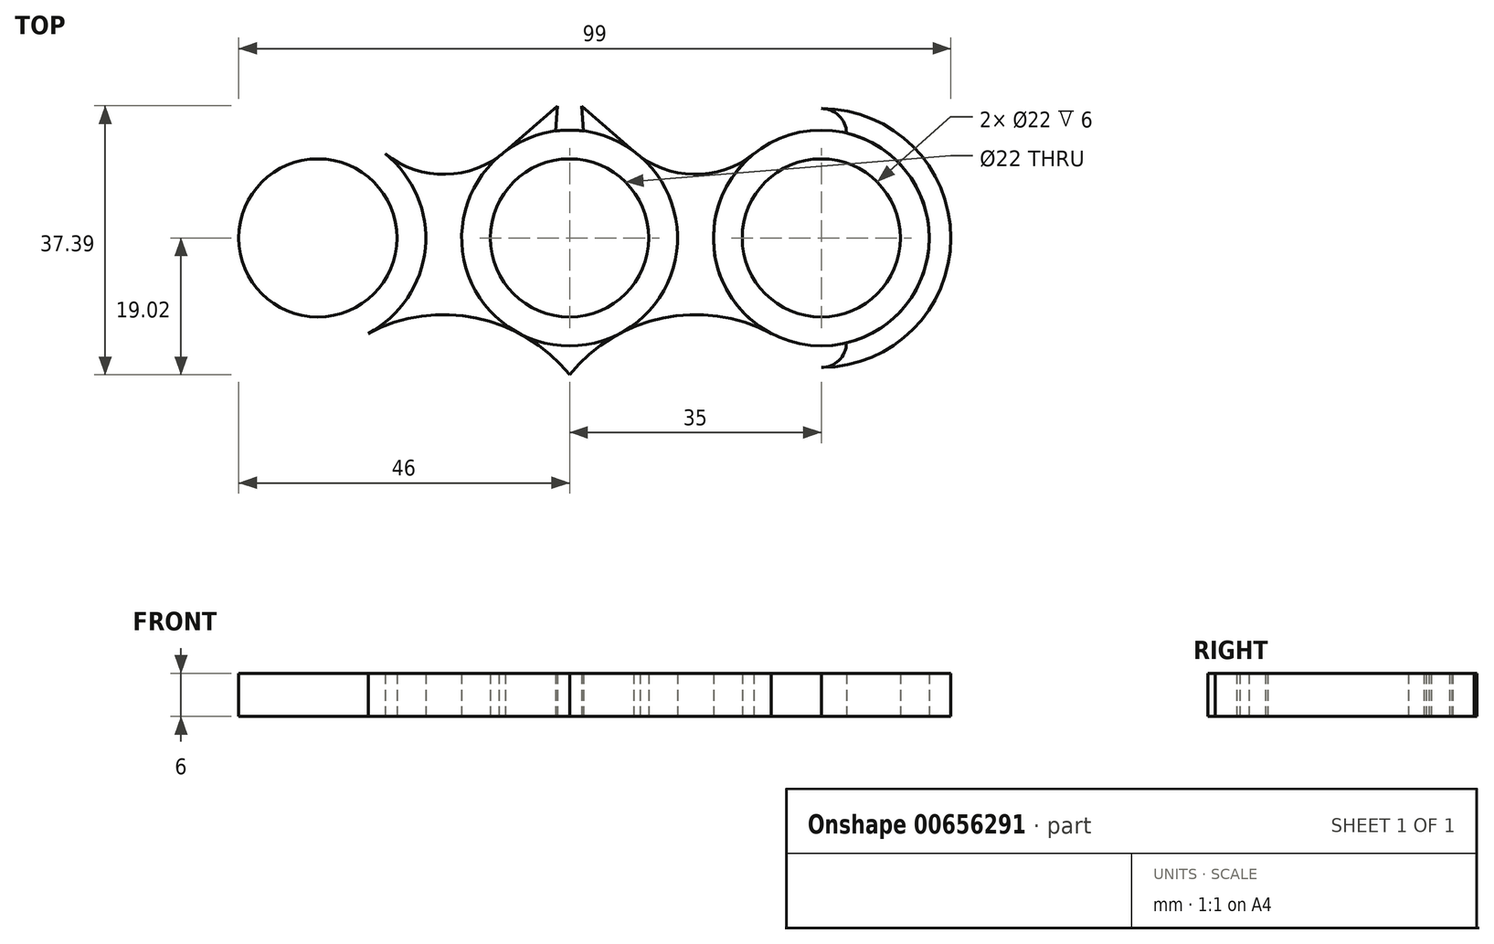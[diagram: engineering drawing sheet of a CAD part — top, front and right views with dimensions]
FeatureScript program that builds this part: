
annotation { "Feature Type Name" : "Feature", "Feature Type Description" : "" }
export const myFeature = defineFeature(function(context is Context, id is Id, definition is map)
    precondition{}
    {
        {
            var Q0;
            Q0=qCreatedBy(makeId("Top.planeOp"),FACE);
            var sketch = newSketch(context, id + "F0", { "sketchPlane" : qUnion([Q0])});
            skCircle(sketch, "E0", {"center": v(0, 0) * mm, "radius": 11 * mm});
            skArc(sketch, "E1", {"start": v(9.79, 11.37) * mm, "mid": v(9.37, 11.71) * mm, "end": v(8.95, 12.04) * mm});
            skLineSegment(sketch, "E2", {"start": v(0, 37.98) * mm, "end": v(0, -39.63) * mm, "construction": true});
            skLineSegment(sketch, "E3", {"start": v(1.92, 14.88) * mm, "end": v(1.68, 18.37) * mm});
            skLineSegment(sketch, "E4", {"start": v(1.68, 18.37) * mm, "end": v(8.95, 12.04) * mm});
            skLineSegment(sketch, "E5.MirrorCS", {"start": v(-1.92, 14.88) * mm, "end": v(-1.68, 18.37) * mm});
            skLineSegment(sketch, "E6.MirrorCS", {"start": v(-1.68, 18.37) * mm, "end": v(-8.95, 12.04) * mm});
            skLineSegment(sketch, "E7", {"start": v(-52.8, 0) * mm, "end": v(68.66, 0) * mm, "construction": true});
            skCircle(sketch, "E8", {"center": v(35, 0) * mm, "radius": 11 * mm});
            skCircle(sketch, "E9.MirrorC", {"center": v(-35, 0) * mm, "radius": 11 * mm});
            skArc(sketch, "E10", {"start": v(28, -13.27) * mm, "mid": v(33.13, -14.88) * mm, "end": v(38.5, -14.59) * mm});
            skArc(sketch, "E11.MirrorC", {"start": v(-38.5, 14.59) * mm, "mid": v(-31.72, 14.64) * mm, "end": v(-25.62, 11.7) * mm});
            skArc(sketch, "E12", {"start": v(8.95, 12.04) * mm, "mid": v(17.22, 8.85) * mm, "end": v(25.62, 11.7) * mm});
            skArc(sketch, "E13.MirrorCS", {"start": v(-8.95, 12.04) * mm, "mid": v(-17.22, 8.85) * mm, "end": v(-25.62, 11.7) * mm});
            skArc(sketch, "E14", {"start": v(0, -19.02) * mm, "mid": v(-12.97, -11.13) * mm, "end": v(-28, -13.27) * mm});
            skArc(sketch, "E15", {"start": v(-20.67, -10.9) * mm, "mid": v(-17.04, -1.14) * mm, "end": v(-19.4, 8.99) * mm});
            skArc(sketch, "E16", {"start": v(-38.5, 14.59) * mm, "mid": v(-37.44, 17) * mm, "end": v(-35, 18) * mm});
            skArc(sketch, "E17.MirrorC", {"start": v(-38.5, -14.59) * mm, "mid": v(-37.44, -17) * mm, "end": v(-35, -18) * mm});
            skArc(sketch, "E18.MirrorC", {"start": v(38.5, 14.59) * mm, "mid": v(37.44, 17) * mm, "end": v(35, 18) * mm});
            skArc(sketch, "E19.MirrorC", {"start": v(38.5, -14.59) * mm, "mid": v(37.44, -17) * mm, "end": v(35, -18) * mm});
            skArc(sketch, "E20.MirrorC", {"start": v(20.67, -10.9) * mm, "mid": v(17.04, -1.14) * mm, "end": v(19.4, 8.99) * mm});
            skArc(sketch, "E21.MirrorCS", {"start": v(0, -19.02) * mm, "mid": v(12.97, -11.13) * mm, "end": v(28, -13.27) * mm});
            skArc(sketch, "E22.trimOffspring", {"start": v(-35, 18) * mm, "mid": v(-53, 0) * mm, "end": v(-35, -18) * mm});
            skArc(sketch, "E23.trimOffspring", {"start": v(-28, -13.27) * mm, "mid": v(-33.13, -14.88) * mm, "end": v(-38.5, -14.59) * mm});
            skArc(sketch, "E24.trimOffspring", {"start": v(35, 18) * mm, "mid": v(53, 0) * mm, "end": v(35, -18) * mm});
            skArc(sketch, "E25.trimOffspring", {"start": v(38.5, 14.59) * mm, "mid": v(31.72, 14.64) * mm, "end": v(25.62, 11.7) * mm});
            skArc(sketch, "E26.trimOffspring", {"start": v(1.92, 14.88) * mm, "mid": v(0, 15) * mm, "end": v(-1.92, 14.88) * mm});
            skCircle(sketch, "E27", {"center": v(0, 0) * mm, "radius": 15 * mm});
            skCircle(sketch, "E28", {"center": v(-35, 0) * mm, "radius": 15 * mm});
            skCircle(sketch, "E29", {"center": v(35, 0) * mm, "radius": 15 * mm});
            skSolve(sketch);
        }
        {
            var Q0;
            Q0=makeQuery(id+"F0.imprint","IMPRINT",FACE,{"disambiguationData":[TD([[makeQuery(id+"F0.imprint","IMPRINT",EDGE,{"derivedFrom":sQuery(id+"F0.wireOp",EDGE,"E0")}),-1.0]])]});
            extrude(context, id + "F1", {"entities" : qUnion([Q0]), "depth" : 6 * mm, "offsetDistance" : 25 * mm});
        }
        {
            var Q0;
            {var subQ0=sQuery(id+"F0.wireOp",EDGE,"E16");Q0=makeQuery(id+"F0.imprint","IMPRINT",FACE,{"disambiguationData":[TD([[makeQuery(id+"F0.imprint","IMPRINT",EDGE,{"derivedFrom":subQ0}),1.0]])]});}
            var Q1;
            {var subQ3=sQuery(id+"F0.wireOp",EDGE,"E15");Q1=makeQuery(id+"F0.imprint","IMPRINT",FACE,{"disambiguationData":[TD([[makeQuery(id+"F0.imprint","IMPRINT",EDGE,{"derivedFrom":subQ3}),1.0]])]});}
            var Q2;
            {var subQ0=sQuery(id+"F0.wireOp",EDGE,"E15");Q2=makeQuery(id+"F0.imprint","IMPRINT",FACE,{"disambiguationData":[TD([[makeQuery(id+"F0.imprint","IMPRINT",EDGE,{"derivedFrom":subQ0}),-1.0]])]});}
            var Q3;
            Q3=makeQuery(id+"F0.imprint","IMPRINT",FACE,{"disambiguationData":[TD([[makeQuery(id+"F0.imprint","IMPRINT",EDGE,{"derivedFrom":sQuery(id+"F0.wireOp",EDGE,"E0")}),-1.0]])]});
            var Q4;
            {var subQ0=sQuery(id+"F0.wireOp",EDGE,"E21.MirrorCS");var subQ1=sQuery(id+"F0.wireOp",EDGE,"E14");var subQ2=makeQuery(id+"F0.imprint","INTERSECT",VERTEX,{"derivedFrom":[subQ1,subQ0]});Q4=makeQuery(id+"F0.imprint","IMPRINT",FACE,{"disambiguationData":[TD([[makeQuery(id+"F0.imprint","IMPRINT",EDGE,{"disambiguationData":[TD([[subQ2,-1.0]])],"derivedFrom":subQ1}),-1.0]])]});}
            var Q5;
            {var subQ0=sQuery(id+"F0.wireOp",EDGE,"E20.MirrorC");Q5=makeQuery(id+"F0.imprint","IMPRINT",FACE,{"disambiguationData":[TD([[makeQuery(id+"F0.imprint","IMPRINT",EDGE,{"derivedFrom":subQ0}),1.0]])]});}
            var Q6;
            {var subQ3=sQuery(id+"F0.wireOp",EDGE,"E20.MirrorC");Q6=makeQuery(id+"F0.imprint","IMPRINT",FACE,{"disambiguationData":[TD([[makeQuery(id+"F0.imprint","IMPRINT",EDGE,{"derivedFrom":subQ3}),-1.0]])]});}
            var Q7;
            {var subQ0=sQuery(id+"F0.wireOp",EDGE,"E18.MirrorC");Q7=makeQuery(id+"F0.imprint","IMPRINT",FACE,{"disambiguationData":[TD([[makeQuery(id+"F0.imprint","IMPRINT",EDGE,{"derivedFrom":subQ0}),-1.0]])]});}
            var Q8;
            {var subQ0=sQuery(id+"F0.wireOp",EDGE,"E5.MirrorCS");Q8=makeQuery(id+"F0.imprint","IMPRINT",FACE,{"disambiguationData":[TD([[makeQuery(id+"F0.imprint","IMPRINT",EDGE,{"derivedFrom":subQ0}),1.0]])]});}
            var Q9;
            {var subQ0=sQuery(id+"F0.wireOp",EDGE,"E3");Q9=makeQuery(id+"F0.imprint","IMPRINT",FACE,{"disambiguationData":[TD([[makeQuery(id+"F0.imprint","IMPRINT",EDGE,{"derivedFrom":subQ0}),-1.0]])]});}
            extrude(context, id + "F2", {"entities" : qUnion([Q0, Q1, Q2, Q3, Q4, Q5, Q6, Q7, Q8, Q9]), "depth" : 6 * mm, "offsetDistance" : 25 * mm});
        }
        {
            var Q0;
            Q0=makeQuery(id+"F0.imprint","IMPRINT",FACE,{"disambiguationData":[TD([[makeQuery(id+"F0.imprint","IMPRINT",EDGE,{"derivedFrom":sQuery(id+"F0.wireOp",EDGE,"E8")}),-1.0]])]});
            var Q1;
            Q1=makeQuery(id+"F0.imprint","IMPRINT",FACE,{"disambiguationData":[TD([[makeQuery(id+"F0.imprint","IMPRINT",EDGE,{"derivedFrom":sQuery(id+"F0.wireOp",EDGE,"E9.MirrorC")}),1.0]])]});
            extrude(context, id + "F3", {"entities" : qUnion([Q0, Q1]), "depth" : 6 * mm, "offsetDistance" : 25 * mm});
        }
    });
